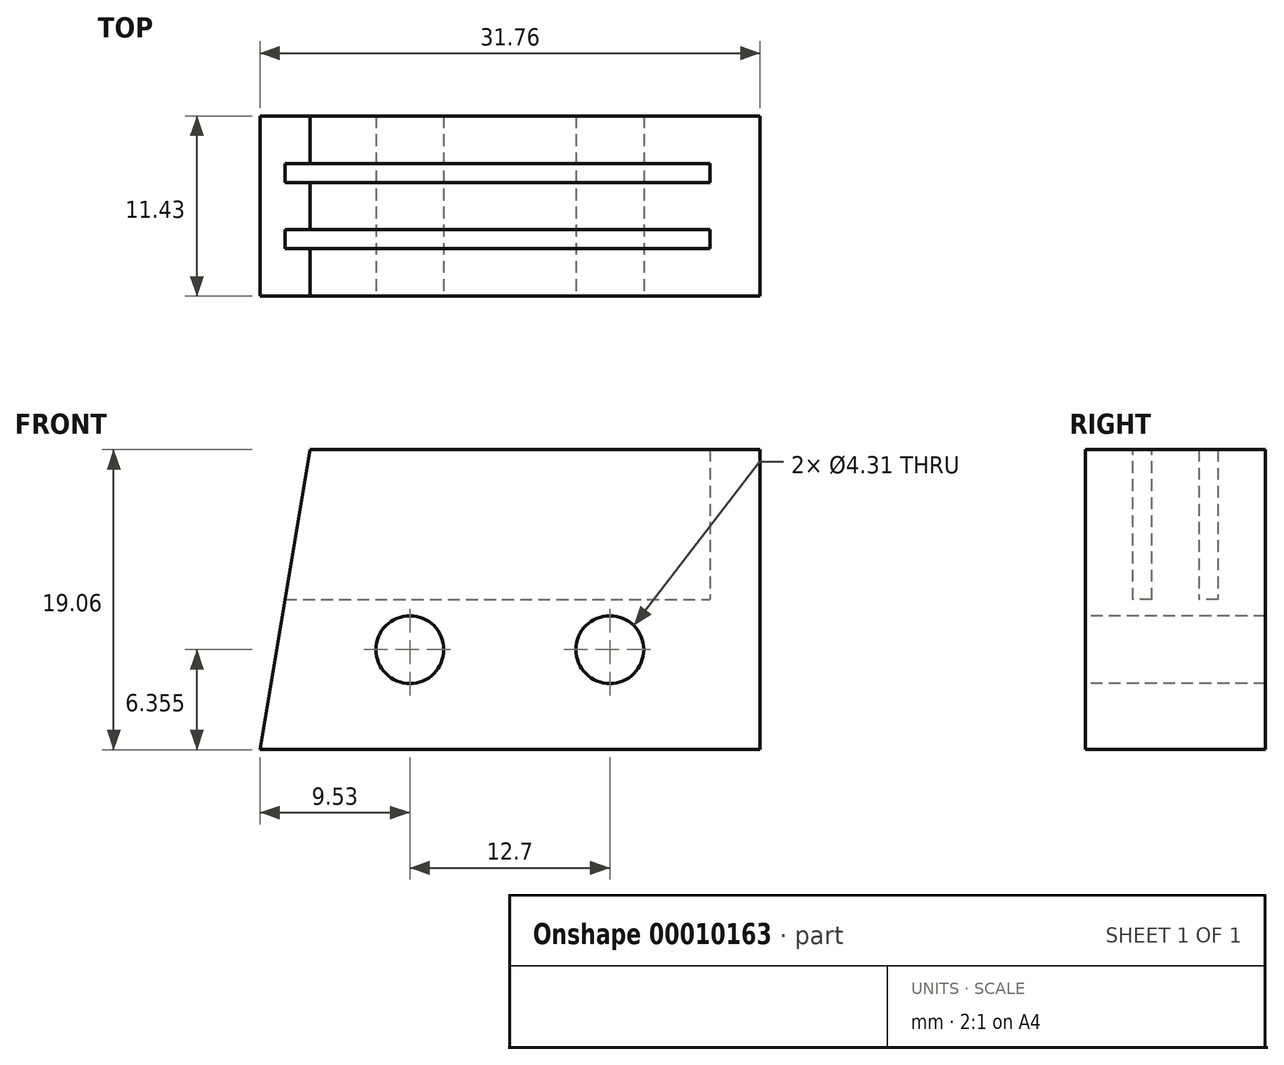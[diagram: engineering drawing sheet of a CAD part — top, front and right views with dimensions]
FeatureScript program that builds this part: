
annotation { "Feature Type Name" : "Feature", "Feature Type Description" : "" }
export const myFeature = defineFeature(function(context is Context, id is Id, definition is map)
    precondition{}
    {
        {
            var Q0;
            Q0=qCreatedBy(makeId("Top.planeOp"),FACE);
            var sketch = newSketch(context, id + "F0", { "sketchPlane" : qUnion([Q0])});
            skLineSegment(sketch, "E0.rect.bottom", {"start": v(15.88, 9.52) * mm, "end": v(-15.88, 9.52) * mm});
            skLineSegment(sketch, "E0.rect.top", {"start": v(15.88, -9.53) * mm, "end": v(-15.88, -9.53) * mm});
            skLineSegment(sketch, "E0.rect.left", {"start": v(15.88, 9.52) * mm, "end": v(15.88, -9.53) * mm});
            skLineSegment(sketch, "E0.rect.right", {"start": v(-15.88, 9.52) * mm, "end": v(-15.88, -9.53) * mm});
            skPoint(sketch, "E0.rect.middle", {"position": v(0, 0) * mm});
            skSolve(sketch);
        }
        {
            var Q0;
            Q0=qSketchRegion(id+"F0",true);
            extrude(context, id + "F1", {"entities" : qUnion([Q0]), "depth" : 11.43 * mm});
        }
        {
            var Q0;
            Q0=makeQuery(id+"F1.opExtrude","CAP_FACE",FACE,{"disambiguationData":[OSD([sQuery(id+"F0.wireOp",EDGE,"E0.rect.bottom"),sQuery(id+"F0.wireOp",EDGE,"E0.rect.top"),sQuery(id+"F0.wireOp",EDGE,"E0.rect.left"),sQuery(id+"F0.wireOp",EDGE,"E0.rect.right")])],"isStart":false});
            var sketch = newSketch(context, id + "F2", { "sketchPlane" : qUnion([Q0])});
            skCircle(sketch, "E1", {"center": v(-6.35, -3.18) * mm, "radius": 2.15 * mm});
            skCircle(sketch, "E2", {"center": v(6.35, -3.18) * mm, "radius": 2.15 * mm});
            skSolve(sketch);
        }
        {
            var Q0;
            Q0=qSketchRegion(id+"F2",true);
            extrude(context, id + "F3", {"entities" : qUnion([Q0]), "operationType" : NewBodyOperationType.REMOVE, "endBound" : BoundingType.UP_TO_NEXT, "oppositeDirection" : true, "depth" : 25.4 * mm});
        }
        {
            var Q0;
            Q0=makeQuery(id+"F1.opExtrude","SWEPT_FACE",FACE,{"disambiguationData":[OSD([sQuery(id+"F0.wireOp",EDGE,"E0.rect.bottom")])]});
            var sketch = newSketch(context, id + "F4", { "sketchPlane" : qUnion([Q0])});
            skLineSegment(sketch, "E3.rect.bottom", {"start": v(19.05, 3.01) * mm, "end": v(-19.05, 3.01) * mm});
            skLineSegment(sketch, "E3.rect.top", {"start": v(19.05, 4.21) * mm, "end": v(-19.05, 4.21) * mm});
            skLineSegment(sketch, "E3.rect.left", {"start": v(19.05, 3.01) * mm, "end": v(19.05, 4.21) * mm});
            skLineSegment(sketch, "E3.rect.right", {"start": v(-19.05, 3.01) * mm, "end": v(-19.05, 4.21) * mm});
            skPoint(sketch, "E3.rect.middle", {"position": v(0, 3.61) * mm});
            skLineSegment(sketch, "E4", {"start": v(-15.88, 5.71) * mm, "end": v(15.88, 5.72) * mm, "construction": true});
            skLineSegment(sketch, "E5.rect.bottom", {"start": v(-15.88, 7.21) * mm, "end": v(15.88, 7.21) * mm});
            skLineSegment(sketch, "E5.rect.top", {"start": v(-15.88, 8.41) * mm, "end": v(15.88, 8.41) * mm});
            skLineSegment(sketch, "E5.rect.left", {"start": v(-15.88, 7.21) * mm, "end": v(-15.88, 8.41) * mm});
            skLineSegment(sketch, "E5.rect.right", {"start": v(15.88, 7.21) * mm, "end": v(15.88, 8.41) * mm});
            skPoint(sketch, "E5.rect.middle", {"position": v(0, 7.81) * mm});
            skSolve(sketch);
        }
        {
            var Q0;
            Q0=qSketchRegion(id+"F4",true);
            extrude(context, id + "F5", {"entities" : qUnion([Q0]), "operationType" : NewBodyOperationType.REMOVE, "oppositeDirection" : true, "depth" : 9.52 * mm});
        }
        {
            var Q0;
            Q0=qCreatedBy(makeId("Front.planeOp"),FACE);
            var sketch = newSketch(context, id + "F6", { "sketchPlane" : qUnion([Q0])});
            skLineSegment(sketch, "E6", {"start": v(77.64, 0) * mm, "end": v(-79.2, 0) * mm, "construction": true});
            skSolve(sketch);
        }
        {
            var Q0;
            Q0=makeQuery(id+"F1.opExtrude","CAP_FACE",FACE,{"disambiguationData":[OSD([sQuery(id+"F0.wireOp",EDGE,"E0.rect.bottom"),sQuery(id+"F0.wireOp",EDGE,"E0.rect.top"),sQuery(id+"F0.wireOp",EDGE,"E0.rect.left"),sQuery(id+"F0.wireOp",EDGE,"E0.rect.right")])],"isStart":false});
            var sketch = newSketch(context, id + "F7", { "sketchPlane" : qUnion([Q0])});
            skLineSegment(sketch, "E7", {"start": v(-15.88, -9.53) * mm, "end": v(-15.88, 9.52) * mm});
            skLineSegment(sketch, "E8", {"start": v(-15.88, 9.52) * mm, "end": v(-12.7, 9.52) * mm});
            skLineSegment(sketch, "E9", {"start": v(-12.7, 9.53) * mm, "end": v(-15.88, -9.53) * mm});
            skSolve(sketch);
        }
        {
            var Q0;
            Q0=qSketchRegion(id+"F7",true);
            var Q1;
            Q1=makeQuery(id+"F1.opExtrude","CAP_FACE",FACE,{"disambiguationData":[OSD([sQuery(id+"F0.wireOp",EDGE,"E0.rect.bottom"),sQuery(id+"F0.wireOp",EDGE,"E0.rect.top"),sQuery(id+"F0.wireOp",EDGE,"E0.rect.left"),sQuery(id+"F0.wireOp",EDGE,"E0.rect.right")])],"isStart":true});
            extrude(context, id + "F8", {"entities" : qUnion([Q0]), "operationType" : NewBodyOperationType.REMOVE, "endBound" : BoundingType.UP_TO_SURFACE, "oppositeDirection" : true, "endBoundEntityFace" : qUnion([Q1]), "depth" : 25.4 * mm});
        }
        {
            var Q0;
            Q0=makeQuery(id+"F1.opExtrude","SWEPT_BODY",BODY,{"disambiguationData":[OSD([sQuery(id+"F0.wireOp",EDGE,"E0.rect.bottom"),sQuery(id+"F0.wireOp",EDGE,"E0.rect.top"),sQuery(id+"F0.wireOp",EDGE,"E0.rect.left"),sQuery(id+"F0.wireOp",EDGE,"E0.rect.right")])]});
            var Q1;
            Q1=sQuery(id+"F6.wireOp",EDGE,"E6");
            transform(context, id + "F9", {"entities" : qUnion([Q0]), "transformType" : TransformType.ROTATION, "transformAxis" : qUnion([Q1]), "angle" : 90 * degree, "oppositeDirection" : true, "makeCopy" : false});
        }
        {
            var Q0;
            Q0=makeQuery(id+"F1.opExtrude","CAP_FACE",FACE,{"disambiguationData":[OSD([sQuery(id+"F0.wireOp",EDGE,"E0.rect.bottom"),sQuery(id+"F0.wireOp",EDGE,"E0.rect.top"),sQuery(id+"F0.wireOp",EDGE,"E0.rect.left"),sQuery(id+"F0.wireOp",EDGE,"E0.rect.right")])],"isStart":false});
            var sketch = newSketch(context, id + "F10", { "sketchPlane" : qUnion([Q0])});
            skLineSegment(sketch, "E10.bottom", {"start": v(15.88, 9.52) * mm, "end": v(12.7, 9.52) * mm});
            skLineSegment(sketch, "E10.top", {"start": v(15.88, -9.53) * mm, "end": v(12.7, -9.53) * mm});
            skLineSegment(sketch, "E10.left", {"start": v(15.88, 9.52) * mm, "end": v(15.88, -9.53) * mm});
            skLineSegment(sketch, "E10.right", {"start": v(12.7, 9.53) * mm, "end": v(12.7, -9.53) * mm});
            skSolve(sketch);
        }
        {
            var Q0;
            Q0 = qSketchRegion(id + "F10", true);
            var Q1;
            Q1=makeQuery(id+"F1.opExtrude","CAP_FACE",FACE,{"disambiguationData":[OSD([sQuery(id+"F0.wireOp",EDGE,"E0.rect.bottom"),sQuery(id+"F0.wireOp",EDGE,"E0.rect.top"),sQuery(id+"F0.wireOp",EDGE,"E0.rect.left"),sQuery(id+"F0.wireOp",EDGE,"E0.rect.right")])],"isStart":true});
            extrude(context, id + "F11", {"entities" : qUnion([Q0]), "operationType" : NewBodyOperationType.ADD, "endBound" : BoundingType.UP_TO_SURFACE, "oppositeDirection" : true, "endBoundEntityFace" : qUnion([Q1]), "depth" : 25.4 * mm});
        }
    });
